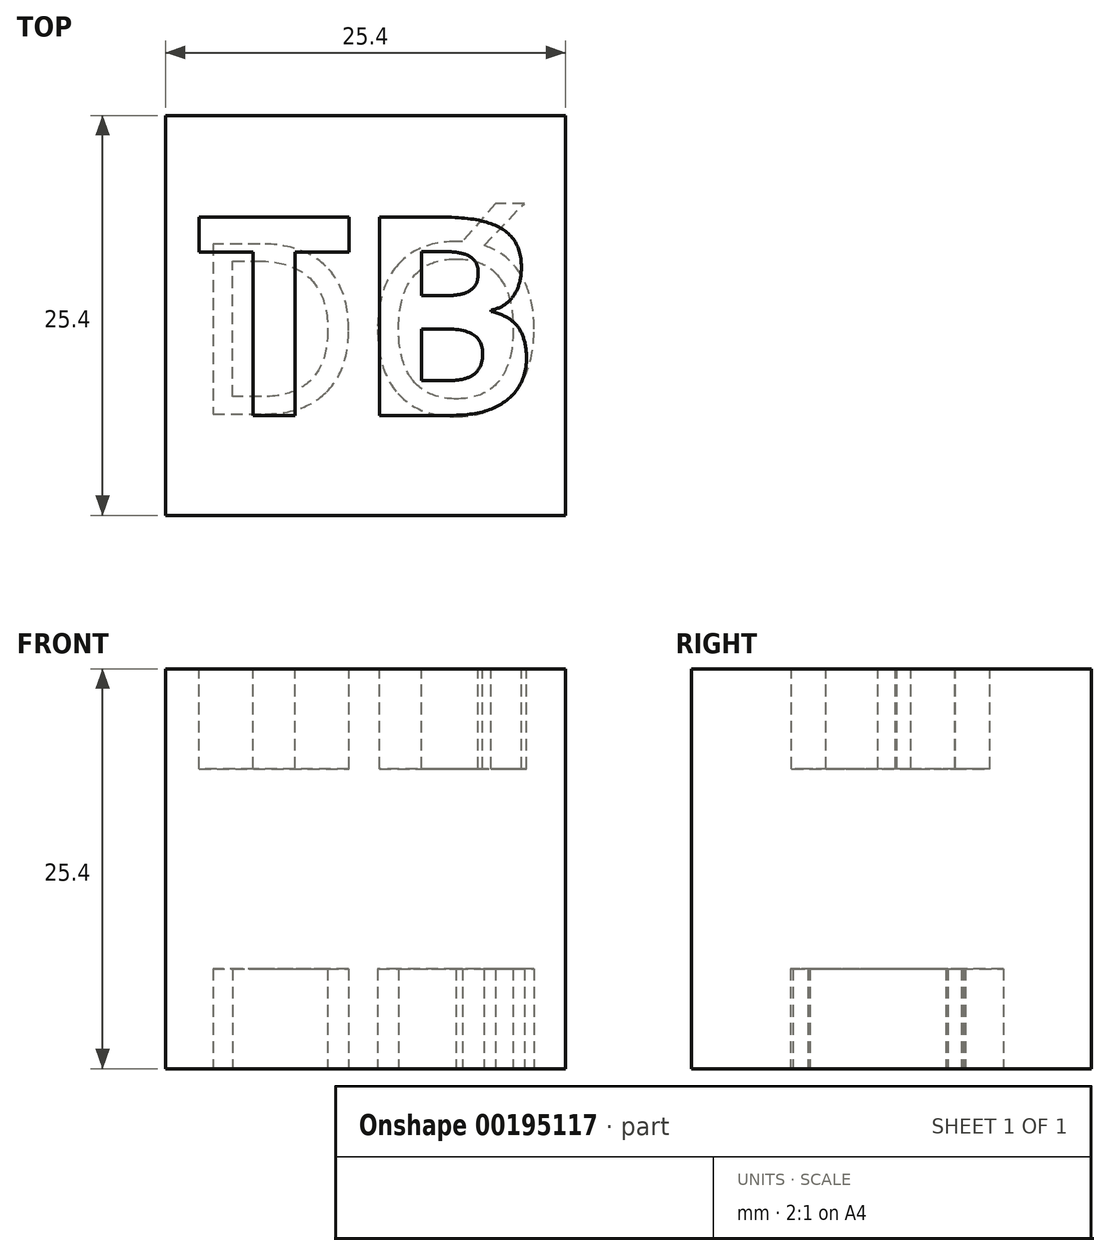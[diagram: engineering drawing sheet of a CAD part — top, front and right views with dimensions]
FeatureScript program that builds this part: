
annotation { "Feature Type Name" : "Feature", "Feature Type Description" : "" }
export const myFeature = defineFeature(function(context is Context, id is Id, definition is map)
    precondition{}
    {
        {
            var Q0;
            Q0=qCreatedBy(makeId("Top.planeOp"),FACE);
            var sketch = newSketch(context, id + "F0", { "sketchPlane" : qUnion([Q0])});
            skLineSegment(sketch, "E0.bottom", {"start": v(0, 0) * mm, "end": v(25.4, 0) * mm});
            skLineSegment(sketch, "E0.top", {"start": v(0, 25.4) * mm, "end": v(25.4, 25.4) * mm});
            skLineSegment(sketch, "E0.left", {"start": v(0, 0) * mm, "end": v(0, 25.4) * mm});
            skLineSegment(sketch, "E0.right", {"start": v(25.4, 0) * mm, "end": v(25.4, 25.4) * mm});
            skSolve(sketch);
        }
        {
            var Q0;
            Q0=makeQuery(id+"F0.imprint","IMPRINT",FACE,{"disambiguationData":[TD([[makeQuery(id+"F0.imprint","IMPRINT",EDGE,{"derivedFrom":sQuery(id+"F0.wireOp",EDGE,"E0.bottom")}),1.0]])]});
            extrude(context, id + "F1", {"entities" : qUnion([Q0]), "depth" : 25.4 * mm});
        }
        {
            var Q0;
            Q0=makeQuery(id+"F1.opExtrude","CAP_FACE",FACE,{"disambiguationData":[OSD([sQuery(id+"F0.wireOp",EDGE,"E0.bottom"),sQuery(id+"F0.wireOp",EDGE,"E0.top"),sQuery(id+"F0.wireOp",EDGE,"E0.left"),sQuery(id+"F0.wireOp",EDGE,"E0.right")])],"isStart":false});
            var sketch = newSketch(context, id + "F2", { "sketchPlane" : qUnion([Q0])});
            skText(sketch, "E1", { "text": "TB", "fontName": "OpenSans-Bold.ttf"});
            const initialGuessF2  = {"E1": [0.00178, 0.00635, 1, 0, 0.0127]};
            skSetInitialGuess(sketch, initialGuessF2);
            skSolve(sketch);
        }
        {
            var Q0;
            Q0 = qSketchRegion(id + "F2", true);
            extrude(context, id + "F3", {"entities" : qUnion([Q0]), "operationType" : NewBodyOperationType.REMOVE, "oppositeDirection" : true, "depth" : 6.35 * mm});
        }
        {
            var Q0;
            Q0=makeQuery(id+"F1.opExtrude","CAP_FACE",FACE,{"disambiguationData":[OSD([sQuery(id+"F0.wireOp",EDGE,"E0.bottom"),sQuery(id+"F0.wireOp",EDGE,"E0.top"),sQuery(id+"F0.wireOp",EDGE,"E0.left"),sQuery(id+"F0.wireOp",EDGE,"E0.right")])],"isStart":true});
            var sketch = newSketch(context, id + "F4", { "sketchPlane" : qUnion([Q0])});
            skText(sketch, "E2", { "text": "DQ", "fontName": "OpenSans-Regular.ttf"});
            const initialGuessF4  = {"E2": [0.00152, -0.01724, 1, 0, 0.01089]};
            skSetInitialGuess(sketch, initialGuessF4);
            skSolve(sketch);
        }
        {
            var Q0;
            Q0 = qSketchRegion(id + "F4", true);
            extrude(context, id + "F5", {"entities" : qUnion([Q0]), "operationType" : NewBodyOperationType.REMOVE, "oppositeDirection" : true, "depth" : 6.35 * mm});
        }
    });
